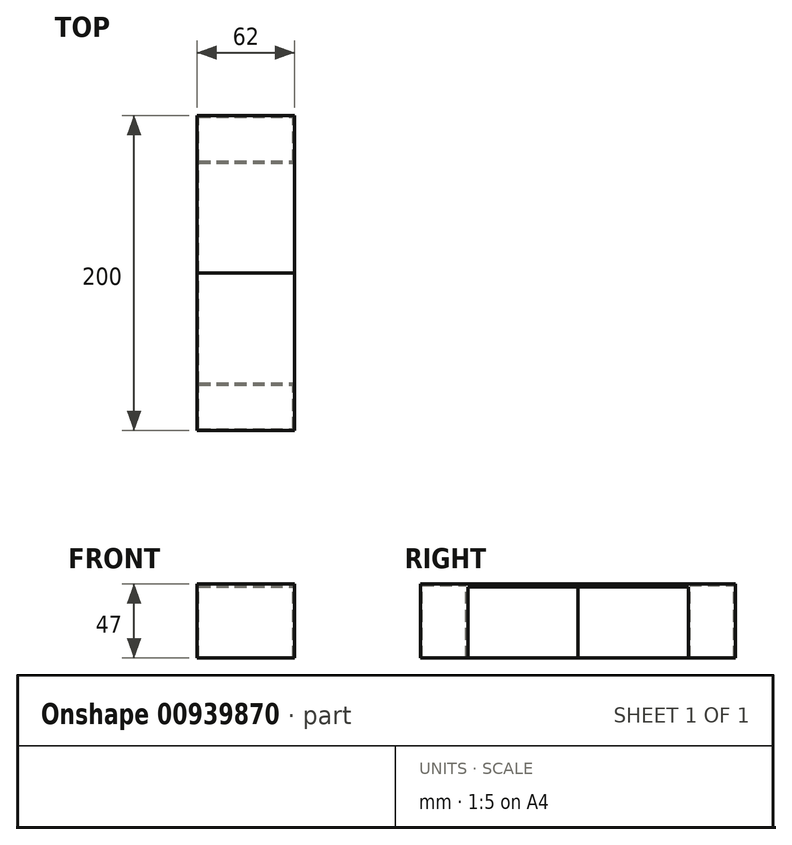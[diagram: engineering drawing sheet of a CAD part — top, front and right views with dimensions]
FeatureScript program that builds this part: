
annotation { "Feature Type Name" : "Feature", "Feature Type Description" : "" }
export const myFeature = defineFeature(function(context is Context, id is Id, definition is map)
    precondition{}
    {
        {
            var Q0;
            Q0=qCreatedBy(makeId("Right.planeOp"),FACE);
            var sketch = newSketch(context, id + "F0", { "sketchPlane" : qUnion([Q0])});
            skLineSegment(sketch, "E0.bottom", {"start": v(-100, 0) * mm, "end": v(100, 0) * mm});
            skLineSegment(sketch, "E0.top", {"start": v(-100, 47) * mm, "end": v(100, 47) * mm});
            skLineSegment(sketch, "E0.left", {"start": v(-100, 0) * mm, "end": v(-100, 47) * mm});
            skLineSegment(sketch, "E0.right", {"start": v(100, 0) * mm, "end": v(100, 47) * mm});
            skSolve(sketch);
        }
        {
            var Q0;
            Q0 = qSketchRegion(id + "F0", true);
            extrude(context, id + "F1", {"entities" : qUnion([Q0]), "oppositeDirection" : true, "depth" : 62 * mm, "offsetDistance" : 25 * mm});
        }
        {
            var Q0;
            Q0=makeQuery(id+"F1.opExtrude","CAP_FACE",FACE,{"disambiguationData":[OSD([sQuery(id+"F0.wireOp",EDGE,"E0.bottom"),sQuery(id+"F0.wireOp",EDGE,"E0.top"),sQuery(id+"F0.wireOp",EDGE,"E0.left"),sQuery(id+"F0.wireOp",EDGE,"E0.right")])],"isStart":true});
            var sketch = newSketch(context, id + "F2", { "sketchPlane" : qUnion([Q0])});
            skLineSegment(sketch, "E1.bottom", {"start": v(-70, 0) * mm, "end": v(70, 0) * mm});
            skLineSegment(sketch, "E1.top", {"start": v(-70, 45) * mm, "end": v(70, 45) * mm});
            skLineSegment(sketch, "E1.left", {"start": v(-70, 0) * mm, "end": v(-70, 45) * mm});
            skLineSegment(sketch, "E1.right", {"start": v(70, 0) * mm, "end": v(70, 45) * mm});
            skSolve(sketch);
        }
        {
            var Q0;
            Q0 = qSketchRegion(id + "F2", true);
            extrude(context, id + "F3", {"entities" : qUnion([Q0]), "operationType" : NewBodyOperationType.REMOVE, "oppositeDirection" : true, "depth" : 61 * mm, "offsetDistance" : 25 * mm});
        }
        {
            var Q0;
            Q0=makeQuery(id+"F1.opExtrude","SWEPT_FACE",FACE,{"disambiguationData":[OSD([sQuery(id+"F0.wireOp",EDGE,"E0.bottom")])]});
            shell(context, id + "F4", {"entities" : qUnion([Q0]), "thickness" : 1 * mm});
        }
        {
            var Q0;
            Q0=makeQuery(id+"F1.opExtrude","SWEPT_FACE",FACE,{"disambiguationData":[OSD([sQuery(id+"F0.wireOp",EDGE,"E0.bottom")])]});
            var sketch = newSketch(context, id + "F5", { "sketchPlane" : qUnion([Q0])});
            skLineSegment(sketch, "E2.bottom", {"start": v(0, 0) * mm, "end": v(-70.88, 0) * mm});
            skLineSegment(sketch, "E2.top", {"start": v(0, 0) * mm, "end": v(-70.88, 0) * mm});
            skLineSegment(sketch, "E2.left", {"start": v(0, 0) * mm, "end": v(0, 0) * mm});
            skLineSegment(sketch, "E2.right", {"start": v(-70.88, 0) * mm, "end": v(-70.88, 0) * mm});
            skSolve(sketch);
        }
        {
            var Q0;
            Q0 = qSketchRegion(id + "F5", true);
            extrude(context, id + "F6", {"entities" : qUnion([Q0]), "operationType" : NewBodyOperationType.REMOVE, "oppositeDirection" : true, "depth" : 120 * mm, "offsetDistance" : 25 * mm});
        }
    });
